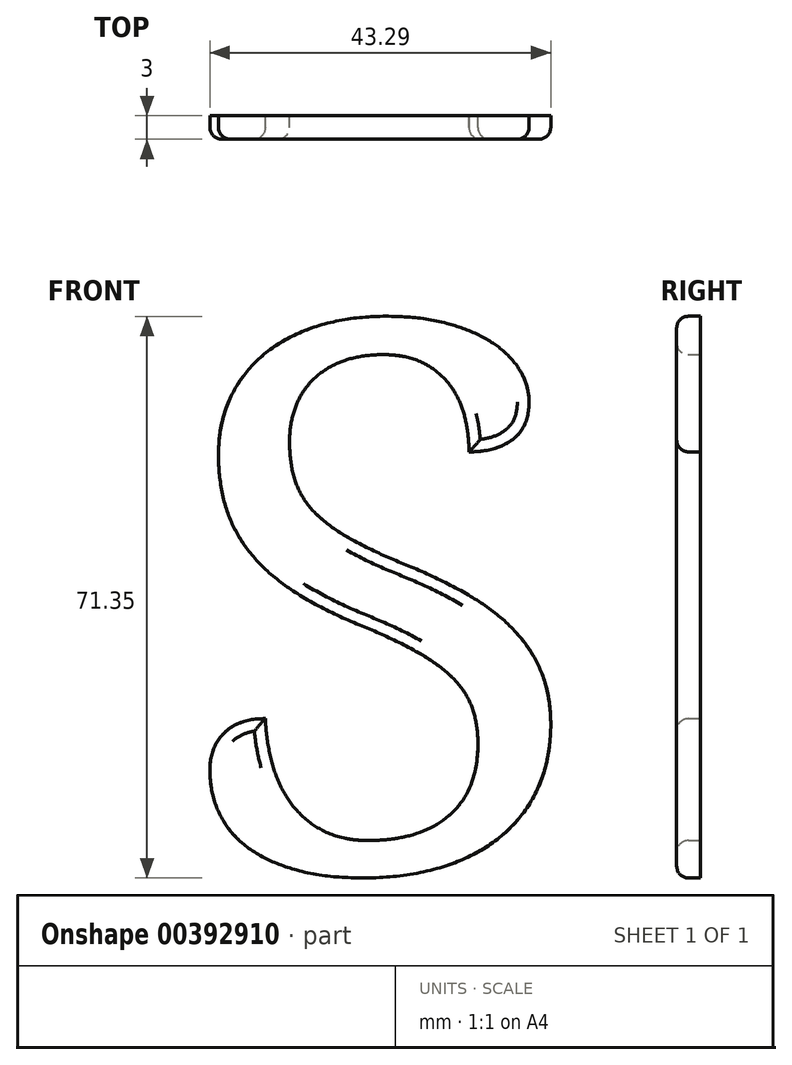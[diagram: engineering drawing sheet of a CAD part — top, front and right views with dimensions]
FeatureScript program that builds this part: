
annotation { "Feature Type Name" : "Feature", "Feature Type Description" : "" }
export const myFeature = defineFeature(function(context is Context, id is Id, definition is map)
    precondition{}
    {
        {
            var Q0;
            Q0=qCreatedBy(makeId("Front.planeOp"),FACE);
            var sketch = newSketch(context, id + "F0", { "sketchPlane" : qUnion([Q0])});
            skText(sketch, "E0", { "text": "S", "fontName": "NotoSerif-Regular.ttf"});
            const initialGuessF0  = {"E0": [0, 0, 1, 0, 0.07]};
            skSetInitialGuess(sketch, initialGuessF0);
            skSolve(sketch);
        }
        {
            var Q0;
            Q0 = qSketchRegion(id + "F0", true);
            extrude(context, id + "F1", {"entities" : qUnion([Q0]), "depth" : 3 * mm});
        }
        {
            var Q0;
            Q0=makeQuery(id+"F1.opExtrude","CAP_FACE",FACE,{"disambiguationData":[OSD([sQuery(id+"F0.wireOp",EDGE,"E0.sketch_text.stroke-0"),sQuery(id+"F0.wireOp",EDGE,"E0.sketch_text.stroke-1"),sQuery(id+"F0.wireOp",EDGE,"E0.sketch_text.stroke-2"),sQuery(id+"F0.wireOp",EDGE,"E0.sketch_text.stroke-3"),sQuery(id+"F0.wireOp",EDGE,"E0.sketch_text.stroke-4"),sQuery(id+"F0.wireOp",EDGE,"E0.sketch_text.stroke-5"),sQuery(id+"F0.wireOp",EDGE,"E0.sketch_text.stroke-6"),sQuery(id+"F0.wireOp",EDGE,"E0.sketch_text.stroke-7"),sQuery(id+"F0.wireOp",EDGE,"E0.sketch_text.stroke-8"),sQuery(id+"F0.wireOp",EDGE,"E0.sketch_text.stroke-9"),sQuery(id+"F0.wireOp",EDGE,"E0.sketch_text.stroke-10"),sQuery(id+"F0.wireOp",EDGE,"E0.sketch_text.stroke-11"),sQuery(id+"F0.wireOp",EDGE,"E0.sketch_text.stroke-12"),sQuery(id+"F0.wireOp",EDGE,"E0.sketch_text.stroke-13"),sQuery(id+"F0.wireOp",EDGE,"E0.sketch_text.stroke-14"),sQuery(id+"F0.wireOp",EDGE,"E0.sketch_text.stroke-15"),sQuery(id+"F0.wireOp",EDGE,"E0.sketch_text.stroke-16"),sQuery(id+"F0.wireOp",EDGE,"E0.sketch_text.stroke-17"),sQuery(id+"F0.wireOp",EDGE,"E0.sketch_text.stroke-18"),sQuery(id+"F0.wireOp",EDGE,"E0.sketch_text.stroke-19"),sQuery(id+"F0.wireOp",EDGE,"E0.sketch_text.stroke-20"),sQuery(id+"F0.wireOp",EDGE,"E0.sketch_text.stroke-21"),sQuery(id+"F0.wireOp",EDGE,"E0.sketch_text.stroke-22"),sQuery(id+"F0.wireOp",EDGE,"E0.sketch_text.stroke-23"),sQuery(id+"F0.wireOp",EDGE,"E0.sketch_text.stroke-24"),sQuery(id+"F0.wireOp",EDGE,"E0.sketch_text.stroke-25"),sQuery(id+"F0.wireOp",EDGE,"E0.sketch_text.stroke-26"),sQuery(id+"F0.wireOp",EDGE,"E0.sketch_text.stroke-27"),sQuery(id+"F0.wireOp",EDGE,"E0.sketch_text.stroke-28"),sQuery(id+"F0.wireOp",EDGE,"E0.sketch_text.stroke-29"),sQuery(id+"F0.wireOp",EDGE,"E0.sketch_text.stroke-30"),sQuery(id+"F0.wireOp",EDGE,"E0.sketch_text.stroke-31"),sQuery(id+"F0.wireOp",EDGE,"E0.sketch_text.stroke-32"),sQuery(id+"F0.wireOp",EDGE,"E0.sketch_text.stroke-33"),sQuery(id+"F0.wireOp",EDGE,"E0.sketch_text.stroke-34"),sQuery(id+"F0.wireOp",EDGE,"E0.sketch_text.stroke-35"),sQuery(id+"F0.wireOp",EDGE,"E0.sketch_text.stroke-36"),sQuery(id+"F0.wireOp",EDGE,"E0.sketch_text.stroke-37"),sQuery(id+"F0.wireOp",EDGE,"E0.sketch_text.stroke-38"),sQuery(id+"F0.wireOp",EDGE,"E0.sketch_text.stroke-39"),sQuery(id+"F0.wireOp",EDGE,"E0.sketch_text.stroke-40"),sQuery(id+"F0.wireOp",EDGE,"E0.sketch_text.stroke-41"),sQuery(id+"F0.wireOp",EDGE,"E0.sketch_text.stroke-42"),sQuery(id+"F0.wireOp",EDGE,"E0.sketch_text.stroke-43"),sQuery(id+"F0.wireOp",EDGE,"E0.sketch_text.stroke-44"),sQuery(id+"F0.wireOp",EDGE,"E0.sketch_text.stroke-45"),sQuery(id+"F0.wireOp",EDGE,"E0.sketch_text.stroke-46"),sQuery(id+"F0.wireOp",EDGE,"E0.sketch_text.stroke-47"),sQuery(id+"F0.wireOp",EDGE,"E0.sketch_text.stroke-48"),sQuery(id+"F0.wireOp",EDGE,"E0.sketch_text.stroke-49"),sQuery(id+"F0.wireOp",EDGE,"E0.sketch_text.stroke-50"),sQuery(id+"F0.wireOp",EDGE,"E0.sketch_text.stroke-51"),sQuery(id+"F0.wireOp",EDGE,"E0.sketch_text.stroke-52"),sQuery(id+"F0.wireOp",EDGE,"E0.sketch_text.stroke-53"),sQuery(id+"F0.wireOp",EDGE,"E0.sketch_text.stroke-54"),sQuery(id+"F0.wireOp",EDGE,"E0.sketch_text.stroke-55")])],"isStart":false});
            fillet(context, id + "F2", {"entities" : qUnion([Q0]), "radius" : 1.5 * mm, "tangentPropagation" : true, "allowEdgeOverflow" : false});
        }
    });
